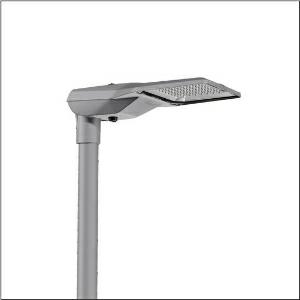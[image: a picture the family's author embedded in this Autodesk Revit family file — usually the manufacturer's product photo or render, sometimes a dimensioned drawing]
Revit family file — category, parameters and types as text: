
# Revit family: streetlight_sl_21_midi___st1_0a_5xe3d43t08nb_3e42
name_source: partatom
category: Lighting Fixtures
units: mm (PartAtom-declared; Revit-internal decimal feet)

## family parameters
Cut with Voids When Loaded = No
Host = Face
Light Source = No
Part Type = Normal
Room Calculation Point = No
Round Connector Dimension = Use Diameter
Shared = No

## types (1)
- --- (1 x LED, 23710 lm, 151.2 W, 4000K)
    Apparent Load = 151 VA
    CIE Flux Codes = 40 73 97 100 100
    Color Rendering = 70
    Color Temperature = 4000K
    Default Elevation = 1800 mm
    Description = Streetlight SL 21 midi, mast luminaire, primary light control with lens, of PMMA, primary optical cover: cover, of toughened safety glass, transparent, light distribution: ST1.0a, light emission: direct distribution, primary light characteristic: asymmetric, installation type: side-entry, post-top, LED, High Power LED, rated luminous flux: 23.710lm, luminous efficacy: 157lm/W, light colour: 740, colour temperature: 4000K, control gear: D4i, control: overheat protection, constant luminous flux control, time-dependent luminous flux control, flexible luminous flux parameterisation, pre-setting: logarithmic dimming characteristic, mains connection: 230..240V, AC, 50/60Hz, start of lifetime: 151W, end of service life: 157W, reduction: 70W, luminaire housing, of diecast aluminium, powder-coated, Siteco® metallic grey (DB 702S), corrosivity category C5 mid according to DIN EN ISO 12944, please order mast flange separately, inclination adjustable: 0°, 5°, 10°, 15°, sealing non-destructively replaceable, multi-level sealing system, length: 644mm, width: 335mm, height: 110mm, mast flange for spigot size: 42mm (side-entry): 5XC10008XM4, 60/48mm (side-entry/post-top): 5XC10108XM2, 76/60mm (side-entry/post-top): 5XC10108XM1, mounting height: 4..8m, Smart Interface below and above, protection rating (complete): IP66, insulation class (complete): insulation class II (safety insulation), certification: CE, ENEC, ENEC+, VDE, impact resistance: IK10, permissible operating ambient temperature for outdoor applications: -40..+50°C, standard-compliant lighting for roads and squares, packaging unit: 1 piece

Light Distribution: ST1.0a
    Height = 111 mm
    Lamp = 1 x LED
    Lamp Light Flux = 23710 lm
    Lamp Power = 151.2 W
    Lamp count = 1
    Length = 644 mm
    Luminous efficacy = 157 lm/W
    Manufacturer = Siteco
    ModVariant = No
    Model = 5XE3D43T08NB
    Number of Poles = 1
    OnlyDefault = Yes
    Power Factor = 1
    Product Name = Streetlight SL 21 midi | ST1.0a
    Product group = mast luminaire | pylon top
    ProductGroupID = 6100
    Protection Class = Protection class II
    Protection Degree = IP 66
    RLX_Detail_Level = 1
    RLX_Emergency_Light_Flux = 0 lm
    RLX_Emergency_Type = 0
    RLX_Emergency_Type_DB = No
    RlxData = <blob elided: 27137 chars, md5=3562d8dd>
    Socket = socket
    Standby Power = 0 W
    System Light Flux = 23710 lm
    System Power = 151 W
    Type Comments = factory setting: luminous flux: 100 % | dim-lin: 254 | 802 mA
    Type Image = l_1004304.jpg
    URL = http://relux.com
    VarID = @adj_191927
    Voltage = 0 V
    Weight = 0.00 kg
    Width = 336 mm

## geometry (parser evidence)
native form markers: Blend x4, Sweep x11
no freeform markers — native parametric forms only
